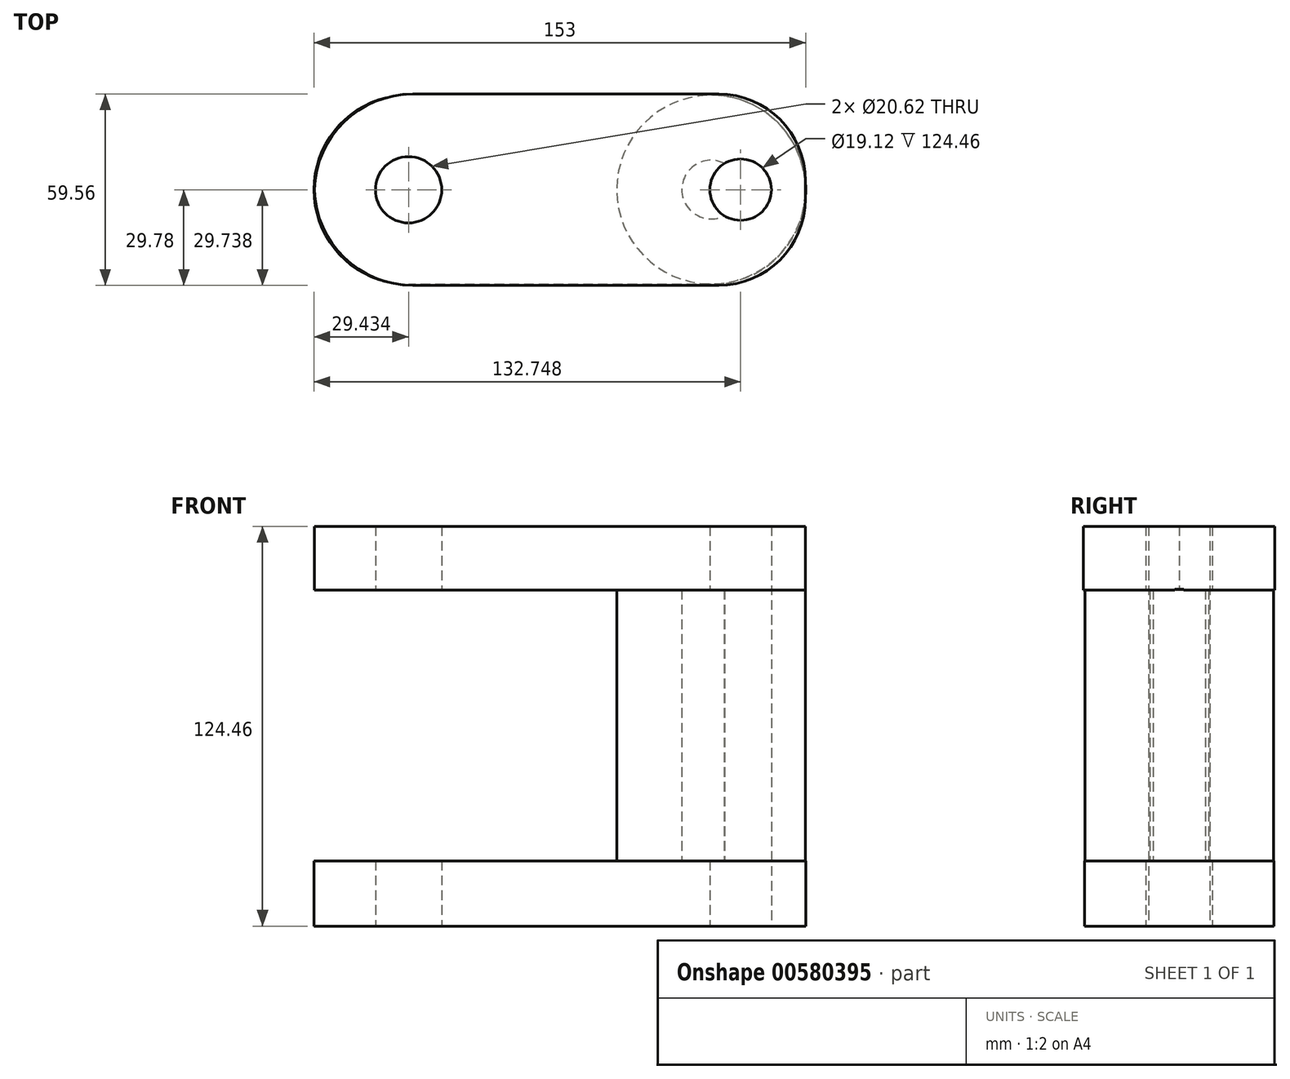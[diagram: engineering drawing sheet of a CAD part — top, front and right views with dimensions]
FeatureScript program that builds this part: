
annotation { "Feature Type Name" : "Feature", "Feature Type Description" : "" }
export const myFeature = defineFeature(function(context is Context, id is Id, definition is map)
    precondition{}
    {
        {
            var Q0;
            Q0=qCreatedBy(makeId("Top.planeOp"),FACE);
            var sketch = newSketch(context, id + "F0", { "sketchPlane" : qUnion([Q0])});
            skLineSegment(sketch, "E0.bottom", {"start": v(76.5, 29.48) * mm, "end": v(-76.5, 29.48) * mm});
            skLineSegment(sketch, "E0.top", {"start": v(76.5, -29.48) * mm, "end": v(-76.5, -29.48) * mm});
            skLineSegment(sketch, "E0.left", {"start": v(76.5, 29.48) * mm, "end": v(76.5, -29.48) * mm});
            skLineSegment(sketch, "E0.right", {"start": v(-76.5, 29.48) * mm, "end": v(-76.5, -29.48) * mm});
            skPoint(sketch, "E0.middle", {"position": v(0, 0) * mm});
            skSolve(sketch);
        }
        {
            var Q0;
            Q0=qSketchRegion(id+"F0",true);
            extrude(context, id + "F1", {"entities" : qUnion([Q0]), "depth" : 20.32 * mm, "offsetDistance" : 25.4 * mm});
        }
        {
            var Q0;
            Q0=makeQuery(id+"F1.opExtrude","SWEPT_EDGE",EDGE,{"disambiguationData":[OSD([sQuery(id+"F0.wireOp",EDGE,"E0.top"),sQuery(id+"F0.wireOp",EDGE,"E0.right")])]});
            var Q1;
            Q1=makeQuery(id+"F1.opExtrude","SWEPT_EDGE",EDGE,{"disambiguationData":[OSD([sQuery(id+"F0.wireOp",EDGE,"E0.bottom"),sQuery(id+"F0.wireOp",EDGE,"E0.right")])]});
            var Q2;
            Q2=makeQuery(id+"F1.opExtrude","SWEPT_EDGE",EDGE,{"disambiguationData":[OSD([sQuery(id+"F0.wireOp",EDGE,"E0.top"),sQuery(id+"F0.wireOp",EDGE,"E0.left")])]});
            var Q3;
            Q3=makeQuery(id+"F1.opExtrude","SWEPT_EDGE",EDGE,{"disambiguationData":[OSD([sQuery(id+"F0.wireOp",EDGE,"E0.bottom"),sQuery(id+"F0.wireOp",EDGE,"E0.left")])]});
            fillet(context, id + "F2", {"entities" : qUnion([Q0, Q1, Q2, Q3]), "radius" : 29.43 * mm, "tangentPropagation" : true, "allowEdgeOverflow" : false});
        }
        {
            var Q0;
            Q0=makeQuery(id+"F1.opExtrude","CAP_FACE",FACE,{"disambiguationData":[OSD([sQuery(id+"F0.wireOp",EDGE,"E0.bottom"),sQuery(id+"F0.wireOp",EDGE,"E0.top"),sQuery(id+"F0.wireOp",EDGE,"E0.left"),sQuery(id+"F0.wireOp",EDGE,"E0.right")])],"isStart":false});
            var sketch = newSketch(context, id + "F3", { "sketchPlane" : qUnion([Q0])});
            skCircle(sketch, "E1", {"center": v(47.07, 0.04) * mm, "radius": 29.37 * mm});
            skCircle(sketch, "E2", {"center": v(47.07, 0.04) * mm, "radius": 9.12 * mm});
            skSolve(sketch);
        }
        {
            var Q0;
            Q0=makeQuery(id+"F3.imprint","IMPRINT",FACE,{"disambiguationData":[TD([[makeQuery(id+"F3.imprint","IMPRINT",EDGE,{"derivedFrom":sQuery(id+"F3.wireOp",EDGE,"E1")}),1.0]])]});
            extrude(context, id + "F4", {"entities" : qUnion([Q0]), "operationType" : NewBodyOperationType.ADD, "depth" : 84.58 * mm, "offsetDistance" : 25.4 * mm});
        }
        {
            var Q0;
            Q0=makeQuery(id+"F4.boolean.opBoolean","SPLIT",FACE,{"disambiguationData":[TD([makeQuery(id+"F4.opExtrude","SWEPT_FACE",FACE,{"disambiguationData":[OSD([sQuery(id+"F3.wireOp",EDGE,"E2")])]})])],"derivedFrom":makeQuery(id+"F1.opExtrude","CAP_FACE",FACE,{"disambiguationData":[OSD([sQuery(id+"F0.wireOp",EDGE,"E0.bottom"),sQuery(id+"F0.wireOp",EDGE,"E0.top"),sQuery(id+"F0.wireOp",EDGE,"E0.left"),sQuery(id+"F0.wireOp",EDGE,"E0.right")])],"isStart":false})});
            extrude(context, id + "F5", {"entities" : qUnion([Q0]), "operationType" : NewBodyOperationType.REMOVE, "endBound" : BoundingType.THROUGH_ALL, "depth" : 25.4 * mm, "offsetDistance" : 25.4 * mm});
        }
        {
            var Q0;
            {var subQ0=sQuery(id+"F0.wireOp",EDGE,"E0.left");var subQ1=sQuery(id+"F0.wireOp",EDGE,"E0.bottom");var subQ2=sQuery(id+"F0.wireOp",EDGE,"E0.top");var subQ3=sQuery(id+"F0.wireOp",EDGE,"E0.right");Q0=makeQuery(id+"F4.boolean.opBoolean","SPLIT",FACE,{"disambiguationData":[TD([makeQuery(id+"F1.opExtrude","SWEPT_FACE",FACE,{"disambiguationData":[OSD([subQ1])]})])],"derivedFrom":makeQuery(id+"F1.opExtrude","CAP_FACE",FACE,{"disambiguationData":[OSD([subQ1,subQ2,subQ0,subQ3])],"isStart":false})});}
            var sketch = newSketch(context, id + "F6", { "sketchPlane" : qUnion([Q0])});
            skCircle(sketch, "E3", {"center": v(-47.07, 0.04) * mm, "radius": 12.08 * mm});
            skSolve(sketch);
        }
        {
            var Q0;
            Q0=makeQuery(id+"F6.imprint","IMPRINT",FACE,{"disambiguationData":[TD([[makeQuery(id+"F6.imprint","IMPRINT",EDGE,{"derivedFrom":sQuery(id+"F6.wireOp",EDGE,"E3")}),1.0]])]});
            extrude(context, id + "F7", {"entities" : qUnion([Q0]), "operationType" : NewBodyOperationType.REMOVE, "endBound" : BoundingType.THROUGH_ALL, "depth" : 25.4 * mm, "offsetDistance" : 25.4 * mm});
        }
        {
            var Q0;
            Q0=qCreatedBy(makeId("Top.planeOp"),FACE);
            cPlane(context, id + "F8", {"entities" : qUnion([Q0]), "cplaneType" : CPlaneType.OFFSET, "offset" : 104.65 * mm, "width" : 152.4 * mm, "height" : 152.4 * mm});
        }
        {
            var Q0;
            Q0=qCreatedBy(id+"F8.planeOp",FACE);
            var sketch = newSketch(context, id + "F9", { "sketchPlane" : qUnion([Q0])});
            skLineSegment(sketch, "E4.bottom", {"start": v(76.4, -29.78) * mm, "end": v(-76.4, -29.78) * mm});
            skLineSegment(sketch, "E4.top", {"start": v(76.4, 29.78) * mm, "end": v(-76.4, 29.78) * mm});
            skLineSegment(sketch, "E4.left", {"start": v(76.4, -29.78) * mm, "end": v(76.4, 29.78) * mm});
            skLineSegment(sketch, "E4.right", {"start": v(-76.4, -29.78) * mm, "end": v(-76.4, 29.78) * mm});
            skPoint(sketch, "E4.middle", {"position": v(0, 0) * mm});
            skSolve(sketch);
        }
        {
            var Q0;
            Q0=makeQuery(id+"F9.imprint","IMPRINT",FACE,{"disambiguationData":[TD([[makeQuery(id+"F9.imprint","IMPRINT",EDGE,{"derivedFrom":sQuery(id+"F9.wireOp",EDGE,"E4.bottom")}),-1.0]])]});
            extrude(context, id + "F10", {"entities" : qUnion([Q0]), "operationType" : NewBodyOperationType.ADD, "depth" : 19.8 * mm, "offsetDistance" : 25.4 * mm});
        }
        {
            var Q0;
            Q0=makeQuery(id+"F1.opExtrude","CAP_FACE",FACE,{"disambiguationData":[OSD([sQuery(id+"F0.wireOp",EDGE,"E0.bottom"),sQuery(id+"F0.wireOp",EDGE,"E0.top"),sQuery(id+"F0.wireOp",EDGE,"E0.left"),sQuery(id+"F0.wireOp",EDGE,"E0.right")])],"isStart":true});
            var sketch = newSketch(context, id + "F11", { "sketchPlane" : qUnion([Q0])});
            skCircle(sketch, "E5", {"center": v(-47.07, 0.04) * mm, "radius": 10.31 * mm});
            skSolve(sketch);
        }
        {
            var Q0;
            Q0=makeQuery(id+"F11.imprint","IMPRINT",FACE,{"disambiguationData":[TD([[makeQuery(id+"F11.imprint","IMPRINT",EDGE,{"derivedFrom":sQuery(id+"F11.wireOp",EDGE,"E5")}),1.0]])]});
            extrude(context, id + "F12", {"entities" : qUnion([Q0]), "operationType" : NewBodyOperationType.REMOVE, "endBound" : BoundingType.THROUGH_ALL, "oppositeDirection" : true, "depth" : 25.4 * mm, "offsetDistance" : 25.4 * mm});
        }
        {
            var Q0;
            Q0=makeQuery(id+"F10.opExtrude","SWEPT_EDGE",EDGE,{"disambiguationData":[OSD([sQuery(id+"F9.wireOp",EDGE,"E4.bottom"),sQuery(id+"F9.wireOp",EDGE,"E4.right")])]});
            var Q1;
            Q1=makeQuery(id+"F10.opExtrude","SWEPT_EDGE",EDGE,{"disambiguationData":[OSD([sQuery(id+"F9.wireOp",EDGE,"E4.top"),sQuery(id+"F9.wireOp",EDGE,"E4.right")])]});
            fillet(context, id + "F13", {"entities" : qUnion([Q0, Q1]), "radius" : 30.66 * mm, "tangentPropagation" : true, "allowEdgeOverflow" : false});
        }
        {
            var Q0;
            Q0=makeQuery(id+"F10.opExtrude","SWEPT_EDGE",EDGE,{"disambiguationData":[OSD([sQuery(id+"F9.wireOp",EDGE,"E4.bottom"),sQuery(id+"F9.wireOp",EDGE,"E4.left")])]});
            var Q1;
            Q1=makeQuery(id+"F10.opExtrude","SWEPT_EDGE",EDGE,{"disambiguationData":[OSD([sQuery(id+"F9.wireOp",EDGE,"E4.top"),sQuery(id+"F9.wireOp",EDGE,"E4.left")])]});
            fillet(context, id + "F14", {"entities" : qUnion([Q0, Q1]), "radius" : 26.98 * mm, "tangentPropagation" : true, "allowEdgeOverflow" : false});
        }
        {
            var Q0;
            Q0=makeQuery(id+"F1.opExtrude","CAP_FACE",FACE,{"disambiguationData":[OSD([sQuery(id+"F0.wireOp",EDGE,"E0.bottom"),sQuery(id+"F0.wireOp",EDGE,"E0.top"),sQuery(id+"F0.wireOp",EDGE,"E0.left"),sQuery(id+"F0.wireOp",EDGE,"E0.right")])],"isStart":true});
            var sketch = newSketch(context, id + "F15", { "sketchPlane" : qUnion([Q0])});
            skCircle(sketch, "E6", {"center": v(56.25, 0) * mm, "radius": 9.56 * mm});
            skSolve(sketch);
        }
        {
            var Q0;
            Q0=makeQuery(id+"F15.imprint","IMPRINT",FACE,{"disambiguationData":[TD([[makeQuery(id+"F15.imprint","IMPRINT",EDGE,{"derivedFrom":sQuery(id+"F15.wireOp",EDGE,"E6")}),1.0]])]});
            extrude(context, id + "F16", {"entities" : qUnion([Q0]), "operationType" : NewBodyOperationType.REMOVE, "endBound" : BoundingType.THROUGH_ALL, "oppositeDirection" : true, "depth" : 25.4 * mm, "offsetDistance" : 25.4 * mm});
        }
    });
